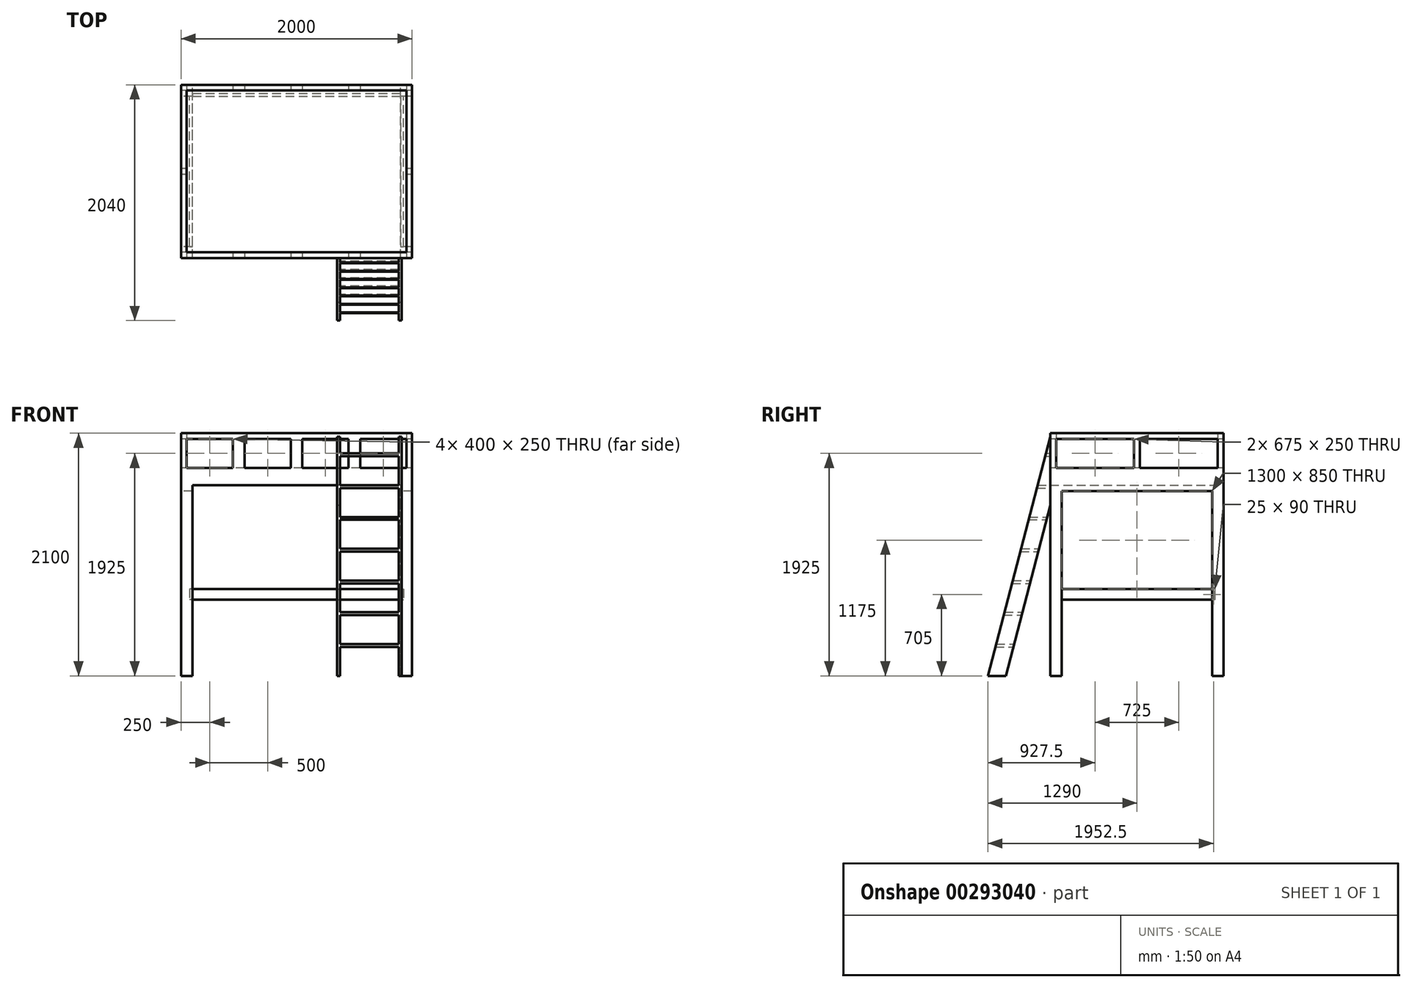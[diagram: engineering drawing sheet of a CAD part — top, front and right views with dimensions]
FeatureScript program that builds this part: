
annotation { "Feature Type Name" : "Feature", "Feature Type Description" : "" }
export const myFeature = defineFeature(function(context is Context, id is Id, definition is map)
    precondition{}
    {
        {
            var Q0;
            Q0=qCreatedBy(makeId("Front.planeOp"),FACE);
            var sketch = newSketch(context, id + "F0", { "sketchPlane" : qUnion([Q0])});
            skLineSegment(sketch, "E0", {"start": v(-1000, 0) * mm, "end": v(-1000, 1800) * mm});
            skLineSegment(sketch, "E1", {"start": v(-1000, 1800) * mm, "end": v(0, 1800) * mm});
            skLineSegment(sketch, "E2", {"start": v(0, 1800) * mm, "end": v(0, -22.44) * mm, "construction": true});
            skLineSegment(sketch, "E3", {"start": v(0, 1800) * mm, "end": v(0, 1650) * mm});
            skLineSegment(sketch, "E4", {"start": v(0, 1650) * mm, "end": v(-900, 1650) * mm});
            skLineSegment(sketch, "E5", {"start": v(-900, 1650) * mm, "end": v(-900, 0) * mm});
            skLineSegment(sketch, "E6", {"start": v(-900, 0) * mm, "end": v(-1000, 0) * mm});
            skSolve(sketch);
        }
        {
            var Q0;
            Q0=qSketchRegion(id+"F0",true);
            extrude(context, id + "F1", {"entities" : qUnion([Q0]), "depth" : 1500 * mm});
        }
        {
            var Q0;
            Q0=makeQuery(id+"F1.opExtrude","SWEPT_BODY",BODY,{"disambiguationData":[OSD([sQuery(id+"F0.wireOp",EDGE,"E0"),sQuery(id+"F0.wireOp",EDGE,"E1"),sQuery(id+"F0.wireOp",EDGE,"E3"),sQuery(id+"F0.wireOp",EDGE,"E4"),sQuery(id+"F0.wireOp",EDGE,"E5"),sQuery(id+"F0.wireOp",EDGE,"E6")])]});
            var Q1;
            Q1=qCreatedBy(makeId("Right.planeOp"),FACE);
            mirror(context, id + "F2", {"operationType" : NewBodyOperationType.ADD, "entities" : qUnion([Q0]), "mirrorPlane" : qUnion([Q1])});
        }
        {
            var Q0;
            {var subQ0=makeQuery(id+"F1.opExtrude","SWEPT_FACE",FACE,{"disambiguationData":[OSD([sQuery(id+"F0.wireOp",EDGE,"E1")])]});Q0=makeQuery(id+"F2.boolean.opBoolean","MERGE",FACE,{"derivedFrom":[subQ0,makeQuery(id+"F2.opPattern","COPY",FACE,{"derivedFrom":subQ0,"instanceName":"1"})]});}
            var sketch = newSketch(context, id + "F3", { "sketchPlane" : qUnion([Q0])});
            skLineSegment(sketch, "E7.bottom", {"start": v(1000, -1500) * mm, "end": v(-1000, -1500) * mm});
            skLineSegment(sketch, "E7.top", {"start": v(1000, 0) * mm, "end": v(-1000, 0) * mm});
            skLineSegment(sketch, "E7.left", {"start": v(1000, -1500) * mm, "end": v(1000, -1450) * mm});
            skLineSegment(sketch, "E7.right", {"start": v(-1000, -1500) * mm, "end": v(-1000, -50) * mm});
            skLineSegment(sketch, "E8", {"start": v(950, -50) * mm, "end": v(-950, -50) * mm});
            skLineSegment(sketch, "E9", {"start": v(-950, -50) * mm, "end": v(-950, -1450) * mm});
            skLineSegment(sketch, "E10", {"start": v(-950, -1450) * mm, "end": v(950, -1450) * mm});
            skLineSegment(sketch, "E11.trimOffspring", {"start": v(-1000, -50) * mm, "end": v(-1000, 0) * mm});
            skLineSegment(sketch, "E12", {"start": v(950, -50) * mm, "end": v(950, -1450) * mm});
            skLineSegment(sketch, "E13", {"start": v(1000, -1450) * mm, "end": v(1000, 0) * mm});
            skSolve(sketch);
        }
        {
            var Q0;
            Q0=qSketchRegion(id+"F3",true);
            extrude(context, id + "F4", {"entities" : qUnion([Q0]), "operationType" : NewBodyOperationType.ADD, "depth" : 300 * mm});
        }
        {
            var Q0;
            {var subQ0=makeQuery(id+"F1.opExtrude","CAP_FACE",FACE,{"disambiguationData":[OSD([sQuery(id+"F0.wireOp",EDGE,"E0"),sQuery(id+"F0.wireOp",EDGE,"E1"),sQuery(id+"F0.wireOp",EDGE,"E3"),sQuery(id+"F0.wireOp",EDGE,"E4"),sQuery(id+"F0.wireOp",EDGE,"E5"),sQuery(id+"F0.wireOp",EDGE,"E6")])],"isStart":false});Q0=makeQuery(id+"F4.boolean.opBoolean","MERGE",FACE,{"derivedFrom":[makeQuery(id+"F2.boolean.opBoolean","MERGE",FACE,{"derivedFrom":[subQ0,makeQuery(id+"F2.opPattern","COPY",FACE,{"derivedFrom":subQ0,"instanceName":"1"})]}),makeQuery(id+"F4.opExtrude","SWEPT_FACE",FACE,{"disambiguationData":[OSD([sQuery(id+"F3.wireOp",EDGE,"E7.bottom")])]})]});}
            var sketch = newSketch(context, id + "F5", { "sketchPlane" : qUnion([Q0])});
            skLineSegment(sketch, "E14.bottom", {"start": v(-950, 2050) * mm, "end": v(-550, 2050) * mm});
            skLineSegment(sketch, "E14.top", {"start": v(-950, 1800) * mm, "end": v(-550, 1800) * mm});
            skLineSegment(sketch, "E14.left", {"start": v(-950, 2050) * mm, "end": v(-950, 1800) * mm});
            skLineSegment(sketch, "E14.right", {"start": v(-550, 2050) * mm, "end": v(-550, 1800) * mm});
            skLineSegment(sketch, "E15.1.0.0", {"start": v(-450, 2050) * mm, "end": v(-450, 1800) * mm});
            skLineSegment(sketch, "E15.1.0.1", {"start": v(-450, 2050) * mm, "end": v(-50, 2050) * mm});
            skLineSegment(sketch, "E15.1.0.2", {"start": v(-50, 2050) * mm, "end": v(-50, 1800) * mm});
            skLineSegment(sketch, "E15.1.0.3", {"start": v(-450, 1800) * mm, "end": v(-50, 1800) * mm});
            skLineSegment(sketch, "E15.2.0.0", {"start": v(50, 2050) * mm, "end": v(50, 1800) * mm});
            skLineSegment(sketch, "E15.2.0.1", {"start": v(50, 2050) * mm, "end": v(450, 2050) * mm});
            skLineSegment(sketch, "E15.2.0.2", {"start": v(450, 2050) * mm, "end": v(450, 1800) * mm});
            skLineSegment(sketch, "E15.2.0.3", {"start": v(50, 1800) * mm, "end": v(450, 1800) * mm});
            skLineSegment(sketch, "E15.direction1", {"start": v(-950, 1800) * mm, "end": v(-450, 1800) * mm, "construction": true});
            skLineSegment(sketch, "E16.0.3.0", {"start": v(550, 2050) * mm, "end": v(550, 1800) * mm});
            skLineSegment(sketch, "E16.3.3.0", {"start": v(550, 2050) * mm, "end": v(950, 2050) * mm});
            skLineSegment(sketch, "E16.6.3.0", {"start": v(950, 2050) * mm, "end": v(950, 1800) * mm});
            skLineSegment(sketch, "E16.9.3.0", {"start": v(550, 1800) * mm, "end": v(950, 1800) * mm});
            skLineSegment(sketch, "E17.0.4.0", {"start": v(1050, 2050) * mm, "end": v(1050, 1800) * mm});
            skLineSegment(sketch, "E17.3.4.0", {"start": v(1050, 2050) * mm, "end": v(1450, 2050) * mm});
            skLineSegment(sketch, "E17.6.4.0", {"start": v(1450, 2050) * mm, "end": v(1450, 1800) * mm});
            skLineSegment(sketch, "E17.9.4.0", {"start": v(1050, 1800) * mm, "end": v(1450, 1800) * mm});
            skSolve(sketch);
        }
        {
            var Q0;
            Q0=qSketchRegion(id+"F5",true);
            extrude(context, id + "F6", {"entities" : qUnion([Q0]), "operationType" : NewBodyOperationType.REMOVE, "endBound" : BoundingType.THROUGH_ALL, "oppositeDirection" : true, "depth" : 25 * mm});
        }
        {
            var Q0;
            Q0=makeQuery(id+"F6.boolean.opBoolean","MERGE",FACE,{"derivedFrom":[makeQuery(id+"F4.opExtrude","SWEPT_FACE",FACE,{"disambiguationData":[OSD([sQuery(id+"F3.wireOp",EDGE,"E9")])]}),makeQuery(id+"F6.opExtrude","SWEPT_FACE",FACE,{"disambiguationData":[OSD([sQuery(id+"F5.wireOp",EDGE,"E14.left")])]})]});
            var sketch = newSketch(context, id + "F7", { "sketchPlane" : qUnion([Q0])});
            skLineSegment(sketch, "E18.bottom", {"start": v(-1450, 2050) * mm, "end": v(-775, 2050) * mm});
            skLineSegment(sketch, "E18.top", {"start": v(-1450, 1800) * mm, "end": v(-775, 1800) * mm});
            skLineSegment(sketch, "E18.left", {"start": v(-1450, 2050) * mm, "end": v(-1450, 1800) * mm});
            skLineSegment(sketch, "E18.right", {"start": v(-775, 2050) * mm, "end": v(-775, 1800) * mm});
            skLineSegment(sketch, "E19.1.0.0", {"start": v(-725, 2050) * mm, "end": v(-725, 1800) * mm});
            skLineSegment(sketch, "E19.1.0.1", {"start": v(-725, 2050) * mm, "end": v(-50, 2050) * mm});
            skLineSegment(sketch, "E19.1.0.2", {"start": v(-50, 2050) * mm, "end": v(-50, 1800) * mm});
            skLineSegment(sketch, "E19.1.0.3", {"start": v(-725, 1800) * mm, "end": v(-50, 1800) * mm});
            skLineSegment(sketch, "E19.direction1", {"start": v(-1450, 1800) * mm, "end": v(-725, 1800) * mm, "construction": true});
            skSolve(sketch);
        }
        {
            var Q0;
            Q0=qSketchRegion(id+"F7",true);
            extrude(context, id + "F8", {"entities" : qUnion([Q0]), "operationType" : NewBodyOperationType.REMOVE, "endBound" : BoundingType.THROUGH_ALL, "depth" : 25 * mm, "hasSecondDirection" : true, "secondDirectionBound" : SecondDirectionBoundingType.THROUGH_ALL, "secondDirectionOppositeDirection" : true, "secondDirectionDepth" : 25 * mm});
        }
        {
            var Q0;
            Q0=makeQuery(id+"F4.boolean.opBoolean","MERGE",FACE,{"derivedFrom":[makeQuery(id+"F1.opExtrude","SWEPT_FACE",FACE,{"disambiguationData":[OSD([sQuery(id+"F0.wireOp",EDGE,"E0")])]}),makeQuery(id+"F4.opExtrude","SWEPT_FACE",FACE,{"disambiguationData":[OSD([sQuery(id+"F3.wireOp",EDGE,"E7.right"),sQuery(id+"F3.wireOp",EDGE,"E11.trimOffspring")])]})]});
            var sketch = newSketch(context, id + "F9", { "sketchPlane" : qUnion([Q0])});
            skLineSegment(sketch, "E20.top", {"start": v(100, 1600) * mm, "end": v(1400, 1600) * mm});
            skLineSegment(sketch, "E20.left", {"start": v(100, 0) * mm, "end": v(100, 1600) * mm});
            skLineSegment(sketch, "E20.right", {"start": v(1400, 0) * mm, "end": v(1400, 1600) * mm});
            skLineSegment(sketch, "E21", {"start": v(100, 0) * mm, "end": v(1400, 0) * mm});
            skSolve(sketch);
        }
        {
            var Q0;
            Q0=makeQuery(id+"F9.imprint","IMPRINT",FACE,{"disambiguationData":[TD([[makeQuery(id+"F9.imprint","IMPRINT",EDGE,{"derivedFrom":sQuery(id+"F9.wireOp",EDGE,"E20.top")}),-1.0]])]});
            extrude(context, id + "F10", {"entities" : qUnion([Q0]), "operationType" : NewBodyOperationType.REMOVE, "endBound" : BoundingType.THROUGH_ALL, "oppositeDirection" : true, "depth" : 25 * mm});
        }
        {
            var Q0;
            Q0=qCreatedBy(makeId("Top.planeOp"),FACE);
            cPlane(context, id + "F11", {"entities" : qUnion([Q0]), "cplaneType" : CPlaneType.OFFSET, "offset" : 660 * mm, "width" : 150 * mm, "height" : 150 * mm});
        }
        {
            var Q0;
            Q0=makeQuery(id+"F1.opExtrude","SWEPT_FACE",FACE,{"disambiguationData":[OSD([sQuery(id+"F0.wireOp",EDGE,"E5")])]});
            cPlane(context, id + "F12", {"entities" : qUnion([Q0]), "cplaneType" : CPlaneType.OFFSET, "offset" : 1250 * mm, "width" : 150 * mm, "height" : 150 * mm});
        }
        {
            var Q0;
            Q0=qCreatedBy(id+"F12.planeOp",FACE);
            var sketch = newSketch(context, id + "F13", { "sketchPlane" : qUnion([Q0])});
            skLineSegment(sketch, "E22", {"start": v(-1500, 2070) * mm, "end": v(-2040, 0) * mm});
            skLineSegment(sketch, "E23", {"start": v(-2040, 0) * mm, "end": v(-1884.98, 0) * mm});
            skLineSegment(sketch, "E24", {"start": v(-1884.98, 0) * mm, "end": v(-1500, 1475.76) * mm});
            skLineSegment(sketch, "E25", {"start": v(-1500, 1475.76) * mm, "end": v(-1500, 2070) * mm});
            skSolve(sketch);
        }
        {
            var Q0;
            Q0=qSketchRegion(id+"F13",true);
            extrude(context, id + "F14", {"entities" : qUnion([Q0]), "depth" : 560 * mm});
        }
        {
            var Q0;
            {var subQ0=makeQuery(id+"F1.opExtrude","CAP_FACE",FACE,{"disambiguationData":[OSD([sQuery(id+"F0.wireOp",EDGE,"E0"),sQuery(id+"F0.wireOp",EDGE,"E1"),sQuery(id+"F0.wireOp",EDGE,"E3"),sQuery(id+"F0.wireOp",EDGE,"E4"),sQuery(id+"F0.wireOp",EDGE,"E5"),sQuery(id+"F0.wireOp",EDGE,"E6")])],"isStart":false});Q0=makeQuery(id+"F4.boolean.opBoolean","MERGE",FACE,{"derivedFrom":[makeQuery(id+"F2.boolean.opBoolean","MERGE",FACE,{"derivedFrom":[subQ0,makeQuery(id+"F2.opPattern","COPY",FACE,{"derivedFrom":subQ0,"instanceName":"1"})]}),makeQuery(id+"F4.opExtrude","SWEPT_FACE",FACE,{"disambiguationData":[OSD([sQuery(id+"F3.wireOp",EDGE,"E7.bottom")])]})]});}
            var sketch = newSketch(context, id + "F15", { "sketchPlane" : qUnion([Q0])});
            skLineSegment(sketch, "E26.bottom", {"start": v(375, 0) * mm, "end": v(885, 0) * mm});
            skLineSegment(sketch, "E26.top", {"start": v(375, 250) * mm, "end": v(885, 250) * mm});
            skLineSegment(sketch, "E26.left", {"start": v(375, 0) * mm, "end": v(375, 250) * mm});
            skLineSegment(sketch, "E26.right", {"start": v(885, 0) * mm, "end": v(885, 250) * mm});
            skLineSegment(sketch, "E27.0.1.0", {"start": v(375, 275) * mm, "end": v(375, 525) * mm});
            skLineSegment(sketch, "E27.0.1.1", {"start": v(375, 525) * mm, "end": v(885, 525) * mm});
            skLineSegment(sketch, "E27.0.1.2", {"start": v(885, 275) * mm, "end": v(885, 525) * mm});
            skLineSegment(sketch, "E27.0.1.3", {"start": v(375, 275) * mm, "end": v(885, 275) * mm});
            skLineSegment(sketch, "E27.0.2.0", {"start": v(375, 550) * mm, "end": v(375, 800) * mm});
            skLineSegment(sketch, "E27.0.2.1", {"start": v(375, 800) * mm, "end": v(885, 800) * mm});
            skLineSegment(sketch, "E27.0.2.2", {"start": v(885, 550) * mm, "end": v(885, 800) * mm});
            skLineSegment(sketch, "E27.0.2.3", {"start": v(375, 550) * mm, "end": v(885, 550) * mm});
            skLineSegment(sketch, "E27.0.3.0", {"start": v(375, 825) * mm, "end": v(375, 1075) * mm});
            skLineSegment(sketch, "E27.0.3.1", {"start": v(375, 1075) * mm, "end": v(885, 1075) * mm});
            skLineSegment(sketch, "E27.0.3.2", {"start": v(885, 825) * mm, "end": v(885, 1075) * mm});
            skLineSegment(sketch, "E27.0.3.3", {"start": v(375, 825) * mm, "end": v(885, 825) * mm});
            skLineSegment(sketch, "E27.0.4.0", {"start": v(375, 1100) * mm, "end": v(375, 1350) * mm});
            skLineSegment(sketch, "E27.0.4.1", {"start": v(375, 1350) * mm, "end": v(885, 1350) * mm});
            skLineSegment(sketch, "E27.0.4.2", {"start": v(885, 1100) * mm, "end": v(885, 1350) * mm});
            skLineSegment(sketch, "E27.0.4.3", {"start": v(375, 1100) * mm, "end": v(885, 1100) * mm});
            skLineSegment(sketch, "E27.0.5.0", {"start": v(375, 1375) * mm, "end": v(375, 1625) * mm});
            skLineSegment(sketch, "E27.0.5.1", {"start": v(375, 1625) * mm, "end": v(885, 1625) * mm});
            skLineSegment(sketch, "E27.0.5.2", {"start": v(885, 1375) * mm, "end": v(885, 1625) * mm});
            skLineSegment(sketch, "E27.0.5.3", {"start": v(375, 1375) * mm, "end": v(885, 1375) * mm});
            skLineSegment(sketch, "E27.0.6.0", {"start": v(375, 1650) * mm, "end": v(375, 1900) * mm});
            skLineSegment(sketch, "E27.0.6.1", {"start": v(375, 1900) * mm, "end": v(885, 1900) * mm});
            skLineSegment(sketch, "E27.0.6.2", {"start": v(885, 1650) * mm, "end": v(885, 1900) * mm});
            skLineSegment(sketch, "E27.0.6.3", {"start": v(375, 1650) * mm, "end": v(885, 1650) * mm});
            skLineSegment(sketch, "E27.0.7.0", {"start": v(375, 1925) * mm, "end": v(375, 2175) * mm});
            skLineSegment(sketch, "E27.0.7.1", {"start": v(375, 2175) * mm, "end": v(885, 2175) * mm});
            skLineSegment(sketch, "E27.0.7.2", {"start": v(885, 1925) * mm, "end": v(885, 2175) * mm});
            skLineSegment(sketch, "E27.0.7.3", {"start": v(375, 1925) * mm, "end": v(885, 1925) * mm});
            skLineSegment(sketch, "E27.direction1", {"start": v(-850, 0) * mm, "end": v(375, 0) * mm, "construction": true});
            skLineSegment(sketch, "E27.direction2", {"start": v(375, 0) * mm, "end": v(375, 275) * mm, "construction": true});
            skSolve(sketch);
        }
        {
            var Q0;
            Q0=qSketchRegion(id+"F15",true);
            extrude(context, id + "F16", {"entities" : qUnion([Q0]), "operationType" : NewBodyOperationType.REMOVE, "endBound" : BoundingType.THROUGH_ALL, "depth" : 25 * mm});
        }
        {
            var Q0;
            Q0=qCreatedBy(id+"F11.planeOp",FACE);
            var sketch = newSketch(context, id + "F17", { "sketchPlane" : qUnion([Q0])});
            skLineSegment(sketch, "E28.bottom", {"start": v(-925, -1400) * mm, "end": v(-900, -1400) * mm});
            skLineSegment(sketch, "E28.top", {"start": v(-925, -75) * mm, "end": v(925, -75) * mm});
            skLineSegment(sketch, "E28.left", {"start": v(-925, -1400) * mm, "end": v(-925, -75) * mm});
            skLineSegment(sketch, "E28.right", {"start": v(925, -1400) * mm, "end": v(925, -75) * mm});
            skLineSegment(sketch, "E29.top", {"start": v(-900, -100) * mm, "end": v(900, -100) * mm});
            skLineSegment(sketch, "E29.left", {"start": v(-900, -1400) * mm, "end": v(-900, -100) * mm});
            skLineSegment(sketch, "E29.right", {"start": v(900, -1400) * mm, "end": v(900, -100) * mm});
            skLineSegment(sketch, "E30.trimOffspring", {"start": v(900, -1400) * mm, "end": v(925, -1400) * mm});
            skSolve(sketch);
        }
        {
            var Q0;
            Q0=qSketchRegion(id+"F17",true);
            extrude(context, id + "F18", {"entities" : qUnion([Q0]), "operationType" : NewBodyOperationType.ADD, "depth" : 90 * mm});
        }
    });
